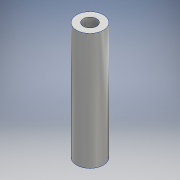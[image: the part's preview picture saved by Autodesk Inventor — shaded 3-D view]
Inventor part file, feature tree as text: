
AUTODESK INVENTOR PART (.ipt)
format: ipt  version: 2016 (Build 200138000, 138)  size: 106,496 bytes
history: native  units: mm
features: sketch x2, extrude x2, hole x2, other x1
ambient origin geometry x8: Origin, YZ Plane, XZ Plane, XY Plane, X Axis, Y Axis, Z Axis, Center Point
bodies: Body1 (feature_tree)
feature tree (7):
  other  "ソリッド1"
  sketch  "スケッチ1"
  extrude  "押し出し1"  Depth=8.0mm
  sketch  "スケッチ2"
  extrude  "押し出し2"  Depth=4.001mm
  hole  "穴1"  [1 undecoded]
  hole  "穴2"  [1 undecoded]
note: 2 required parameter values undecoded (feature->parameter linkage not recoverable at this tier; creation-order binding heuristic only, values carry confidence <= 0.55)
